# Revit family: P500305-109
name_source: partatom
category: Lighting Fixtures
units: mm (PartAtom-declared; Revit-internal decimal feet)

## family parameters
Cut with Voids When Loaded = No
Host = Face
Light Source = No
OmniClass Number = 23.80.70.11.14.17
OmniClass Title = Direct/Indirect
Part Type = Normal
Room Calculation Point = No
Round Connector Dimension = Use Diameter
Shared = Yes

## types (1)
- P500305-109
    Apparent Load = 75 VA
    Assembly Code = D5020200
    Connector Description = Lighting Connector
    Default Elevation = 48 "
    Description = Elevate Collection Four-Light Brushed Bronze and Etched White Glass Modern Style Hanging Pendant Light
    Features = Application: Achieve a sleek and modern look with the Elevate Collection 4-Light Brushed Bronze Etched Glass Modern Pendant Hanging Light ideal for any foyer, dining room, kitchen, breakfast nook, entryway, living room, or stairway.
Styles: Perfect for contemporary, modern, and transitional style settings.
Finish: An angular frame coated in a golden brushed bronze finish that accentuates the design's modern aesthetic.
Materials: Constructed from steel to ensure a long product lifespan.
Glass/Shades: The frame captures the crisp etched white glass cylindrical shades for elegant illumination.
Bulbs: For ideal illumination, use 4 medium base bulbs that are sold separately (75w max - LED/CFL/incandescent). Compatible with dimmable bulbs.
Dimensions: Measures 20-inch diameter by 30-inch height.
Certifications: cULus dry location listed.
Pairs With: Pairs with the Ratio and Mod collections from Progress Lighting.
Warranty: Our 1-Year Limited Warranty guarantees your complete satisfaction with your purchase and includes professional after-sales customer service support.
    Fixture distribution = Direct
    Glass = Glass - Hubbell - Glass
    Gold = Hubbell - Gold
    Housing Material = Hubbell - Brushed Bronze
    Lamp = LED/CFL/incandescent
    Load Classification = Lighting
    Manufacturer = Progress Lighting
    Model = P500305-109
    Power Factor = 1
    Product Documentation Link = https://hubbellcdn.com
    Product Link = https://www.hubbell.com
    Reflector = Glass - Hubbell - Glass
    Texture = Hubbell Textured Wood
    URL = https://www.hubbell.com
    Voltage = 120 V
    Warranty = 1 year Warranty
    Wattage Comments = 75W
    Watts = 75 W

## geometry (parser evidence)
native form markers: Sweep x7
no freeform markers — native parametric forms only
